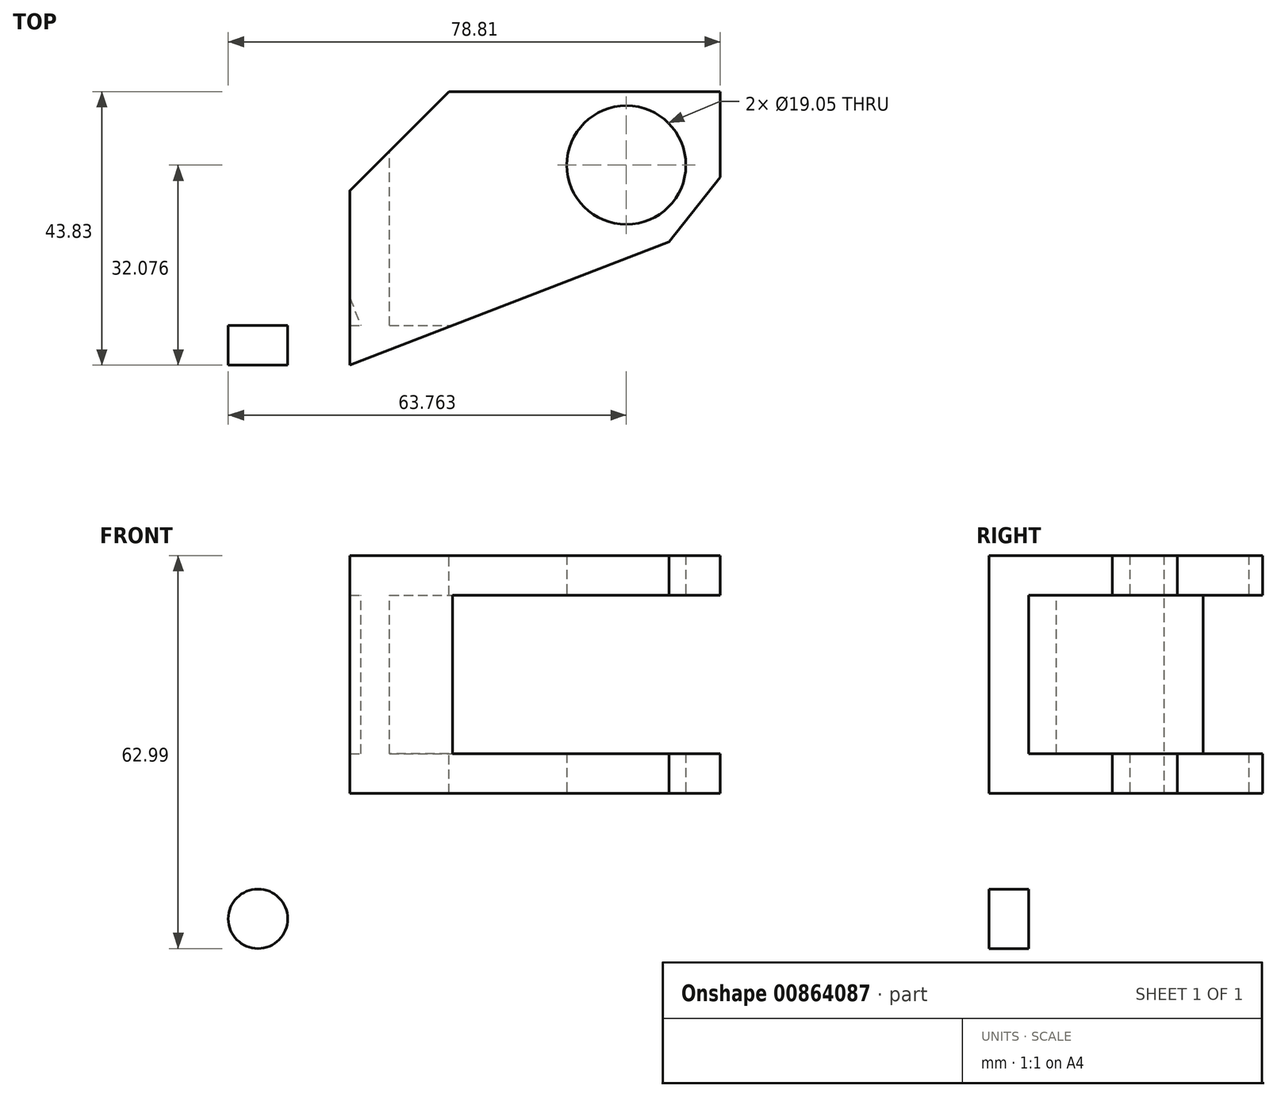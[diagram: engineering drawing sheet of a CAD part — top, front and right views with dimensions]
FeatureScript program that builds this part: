
annotation { "Feature Type Name" : "Feature", "Feature Type Description" : "" }
export const myFeature = defineFeature(function(context is Context, id is Id, definition is map)
    precondition{}
    {
        {
            var Q0;
            Q0=qCreatedBy(makeId("Top.planeOp"),FACE);
            var sketch = newSketch(context, id + "F0", { "sketchPlane" : qUnion([Q0])});
            skCircle(sketch, "E0", {"center": v(0, 0) * mm, "radius": 19.05 * mm});
            skLineSegment(sketch, "E1.bottom", {"start": v(57.15, -95.87) * mm, "end": v(-57.15, -95.87) * mm});
            skLineSegment(sketch, "E1.top", {"start": v(57.15, 95.87) * mm, "end": v(-57.15, 95.87) * mm});
            skLineSegment(sketch, "E1.left", {"start": v(57.15, -95.87) * mm, "end": v(57.15, 95.87) * mm});
            skLineSegment(sketch, "E1.right", {"start": v(-57.15, -95.87) * mm, "end": v(-57.15, 95.87) * mm});
            skLineSegment(sketch, "E2", {"start": v(57.15, 33.03) * mm, "end": v(-57.15, 33.03) * mm});
            skLineSegment(sketch, "E3", {"start": v(57.15, -43.83) * mm, "end": v(-57.15, -43.83) * mm});
            skLineSegment(sketch, "E4", {"start": v(57.15, -43.83) * mm, "end": v(108.3, -24.07) * mm});
            skLineSegment(sketch, "E5", {"start": v(108.3, -24.07) * mm, "end": v(116.49, -13.71) * mm});
            skLineSegment(sketch, "E6", {"start": v(116.49, -13.71) * mm, "end": v(116.49, 0) * mm});
            skLineSegment(sketch, "E7", {"start": v(116.49, 0) * mm, "end": v(57.15, 0) * mm});
            skLineSegment(sketch, "E8", {"start": v(-37.76, 33.03) * mm, "end": v(-57.15, -15.83) * mm});
            skLineSegment(sketch, "E9.MirrorCS", {"start": v(37.76, 33.03) * mm, "end": v(57.15, -15.83) * mm});
            skSolve(sketch);
        }
        {
            var Q0;
            Q0=makeQuery(id+"F0.imprint","IMPRINT",FACE,{"disambiguationData":[TD([[makeQuery(id+"F0.imprint","IMPRINT",EDGE,{"derivedFrom":sQuery(id+"F0.wireOp",EDGE,"E0")}),-1.0]])]});
            extrude(context, id + "F1", {"entities" : qUnion([Q0]), "depth" : 152.4 * mm, "offsetDistance" : 25.4 * mm, "symmetric" : true});
        }
        {
            var Q0;
            {var subQ0=sQuery(id+"F0.wireOp",EDGE,"E4");Q0=makeQuery(id+"F0.imprint","IMPRINT",FACE,{"disambiguationData":[TD([[makeQuery(id+"F0.imprint","IMPRINT",EDGE,{"derivedFrom":subQ0}),1.0]])]});}
            extrude(context, id + "F2", {"entities" : qUnion([Q0]), "operationType" : NewBodyOperationType.ADD, "depth" : 38.1 * mm, "offsetDistance" : 25.4 * mm, "symmetric" : true});
        }
        {
            var Q0;
            Q0=makeQuery(id+"F2.opExtrude","SWEPT_FACE",FACE,{"disambiguationData":[OSD([sQuery(id+"F0.wireOp",EDGE,"E7")])]});
            var Q1;
            Q1=makeQuery(id+"F2.opExtrude","SWEPT_FACE",FACE,{"disambiguationData":[OSD([sQuery(id+"F0.wireOp",EDGE,"E6")])]});
            var Q2;
            Q2=makeQuery(id+"F2.opExtrude","SWEPT_FACE",FACE,{"disambiguationData":[OSD([sQuery(id+"F0.wireOp",EDGE,"E5")])]});
            var Q3;
            Q3=makeQuery(id+"F2.opExtrude","SWEPT_FACE",FACE,{"disambiguationData":[OSD([sQuery(id+"F0.wireOp",EDGE,"E4")])]});
            shell(context, id + "F3", {"entities" : qUnion([Q0, Q1, Q2, Q3]), "thickness" : 6.35 * mm});
        }
        {
            var Q0;
            Q0=makeQuery(id+"F2.opExtrude","CAP_FACE",FACE,{"disambiguationData":[OSD([sQuery(id+"F0.wireOp",EDGE,"E1.left"),sQuery(id+"F0.wireOp",EDGE,"E4"),sQuery(id+"F0.wireOp",EDGE,"E5"),sQuery(id+"F0.wireOp",EDGE,"E6"),sQuery(id+"F0.wireOp",EDGE,"E7")])],"isStart":true});
            var sketch = newSketch(context, id + "F4", { "sketchPlane" : qUnion([Q0])});
            skCircle(sketch, "E10", {"center": v(101.44, 11.75) * mm, "radius": 9.53 * mm});
            skSolve(sketch);
        }
        {
            var Q0;
            Q0=makeQuery(id+"F4.imprint","IMPRINT",FACE,{"disambiguationData":[TD([[makeQuery(id+"F4.imprint","IMPRINT",EDGE,{"derivedFrom":sQuery(id+"F4.wireOp",EDGE,"E10")}),1.0]])]});
            extrude(context, id + "F5", {"entities" : qUnion([Q0]), "operationType" : NewBodyOperationType.REMOVE, "endBound" : BoundingType.THROUGH_ALL, "oppositeDirection" : true, "depth" : 25.4 * mm, "offsetDistance" : 25.4 * mm});
        }
        {
            var Q0;
            {var subQ2=sQuery(id+"F0.wireOp",EDGE,"E9.MirrorCS");Q0=makeQuery(id+"F0.imprint","IMPRINT",FACE,{"disambiguationData":[TD([[makeQuery(id+"F0.imprint","IMPRINT",EDGE,{"derivedFrom":subQ2}),1.0]])]});}
            var Q1;
            {var subQ3=sQuery(id+"F0.wireOp",EDGE,"E8");Q1=makeQuery(id+"F0.imprint","IMPRINT",FACE,{"disambiguationData":[TD([[makeQuery(id+"F0.imprint","IMPRINT",EDGE,{"derivedFrom":subQ3}),-1.0]])]});}
            extrude(context, id + "F6", {"entities" : qUnion([Q0, Q1]), "operationType" : NewBodyOperationType.REMOVE, "oppositeDirection" : true, "depth" : 254 * mm, "offsetDistance" : 25.4 * mm, "symmetric" : true});
        }
        {
            var Q0;
            Q0=makeQuery(id+"F2.opExtrude","SWEPT_EDGE",EDGE,{"disambiguationData":[OSD([sQuery(id+"F0.wireOp",EDGE,"E1.left"),sQuery(id+"F0.wireOp",EDGE,"E7")])]});
            chamfer(context, id + "F7", {"entities" : qUnion([Q0]), "width" : 15.88 * mm, "tangentPropagation" : true});
        }
        {
            var Q0;
            Q0=makeQuery(id+"F1.opExtrude","SWEPT_FACE",FACE,{"disambiguationData":[OSD([sQuery(id+"F0.wireOp",EDGE,"E1.right")])]});
            var sketch = newSketch(context, id + "F8", { "sketchPlane" : qUnion([Q0])});
            skLineSegment(sketch, "E11.bottom", {"start": v(63.5, 63.5) * mm, "end": v(-63.5, 63.5) * mm});
            skLineSegment(sketch, "E11.top", {"start": v(63.5, -63.5) * mm, "end": v(-63.5, -63.5) * mm});
            skLineSegment(sketch, "E11.left", {"start": v(63.5, 63.5) * mm, "end": v(63.5, -63.5) * mm});
            skLineSegment(sketch, "E11.right", {"start": v(-63.5, 63.5) * mm, "end": v(-63.5, -63.5) * mm});
            skPoint(sketch, "E11.middle", {"position": v(0, 0) * mm});
            skLineSegment(sketch, "E12", {"start": v(-14.1, 63.5) * mm, "end": v(-14.1, -63.5) * mm});
            skSolve(sketch);
        }
        {
            var Q0;
            {var subQ0=sQuery(id+"F8.wireOp",EDGE,"E12");Q0=makeQuery(id+"F8.imprint","IMPRINT",FACE,{"disambiguationData":[TD([[makeQuery(id+"F8.imprint","IMPRINT",EDGE,{"derivedFrom":subQ0}),1.0]])]});}
            var Q1;
            {var subQ0=sQuery(id+"F8.wireOp",EDGE,"E11.right");Q1=makeQuery(id+"F8.imprint","IMPRINT",FACE,{"disambiguationData":[TD([[makeQuery(id+"F8.imprint","IMPRINT",EDGE,{"derivedFrom":subQ0}),1.0]])]});}
            extrude(context, id + "F9", {"entities" : qUnion([Q0, Q1]), "operationType" : NewBodyOperationType.REMOVE, "oppositeDirection" : true, "depth" : 114.3 * mm, "offsetDistance" : 25.4 * mm});
        }
        {
            var Q0;
            Q0=makeQuery(id+"F1.opExtrude","SWEPT_FACE",FACE,{"disambiguationData":[OSD([sQuery(id+"F0.wireOp",EDGE,"E3")])]});
            var sketch = newSketch(context, id + "F10", { "sketchPlane" : qUnion([Q0])});
            skCircle(sketch, "E13", {"center": v(0, 0) * mm, "radius": 44.45 * mm});
            skSolve(sketch);
        }
        {
            var Q0;
            Q0=makeQuery(id+"F10.imprint","IMPRINT",FACE,{"disambiguationData":[TD([[makeQuery(id+"F10.imprint","IMPRINT",EDGE,{"derivedFrom":sQuery(id+"F10.wireOp",EDGE,"E13")}),1.0]])]});
            extrude(context, id + "F11", {"entities" : qUnion([Q0]), "operationType" : NewBodyOperationType.REMOVE, "endBound" : BoundingType.THROUGH_ALL, "oppositeDirection" : true, "depth" : 25.4 * mm, "offsetDistance" : 25.4 * mm});
        }
        {
            var Q0;
            Q0=makeQuery(id+"F1.opExtrude","SWEPT_FACE",FACE,{"disambiguationData":[OSD([sQuery(id+"F0.wireOp",EDGE,"E3")])]});
            var sketch = newSketch(context, id + "F12", { "sketchPlane" : qUnion([Q0])});
            skCircle(sketch, "E14", {"center": v(0, 58.9) * mm, "radius": 4.76 * mm});
            skCircle(sketch, "E15", {"center": v(-42.45, -39.18) * mm, "radius": 4.76 * mm});
            skCircle(sketch, "E16.MirrorC", {"center": v(42.45, -39.18) * mm, "radius": 4.76 * mm});
            skSolve(sketch);
        }
        {
            var Q0;
            Q0=makeQuery(id+"F12.imprint","IMPRINT",FACE,{"disambiguationData":[TD([[makeQuery(id+"F12.imprint","IMPRINT",EDGE,{"derivedFrom":sQuery(id+"F12.wireOp",EDGE,"E15")}),1.0]])]});
            var Q1;
            Q1=makeQuery(id+"F12.imprint","IMPRINT",FACE,{"disambiguationData":[TD([[makeQuery(id+"F12.imprint","IMPRINT",EDGE,{"derivedFrom":sQuery(id+"F12.wireOp",EDGE,"E16.MirrorC")}),-1.0]])]});
            var Q2;
            Q2=makeQuery(id+"F12.imprint","IMPRINT",FACE,{"disambiguationData":[TD([[makeQuery(id+"F12.imprint","IMPRINT",EDGE,{"derivedFrom":sQuery(id+"F12.wireOp",EDGE,"E14")}),1.0]])]});
            extrude(context, id + "F13", {"entities" : qUnion([Q0, Q1, Q2]), "operationType" : NewBodyOperationType.REMOVE, "endBound" : BoundingType.THROUGH_ALL, "oppositeDirection" : true, "depth" : 25.4 * mm, "offsetDistance" : 25.4 * mm});
        }
    });
